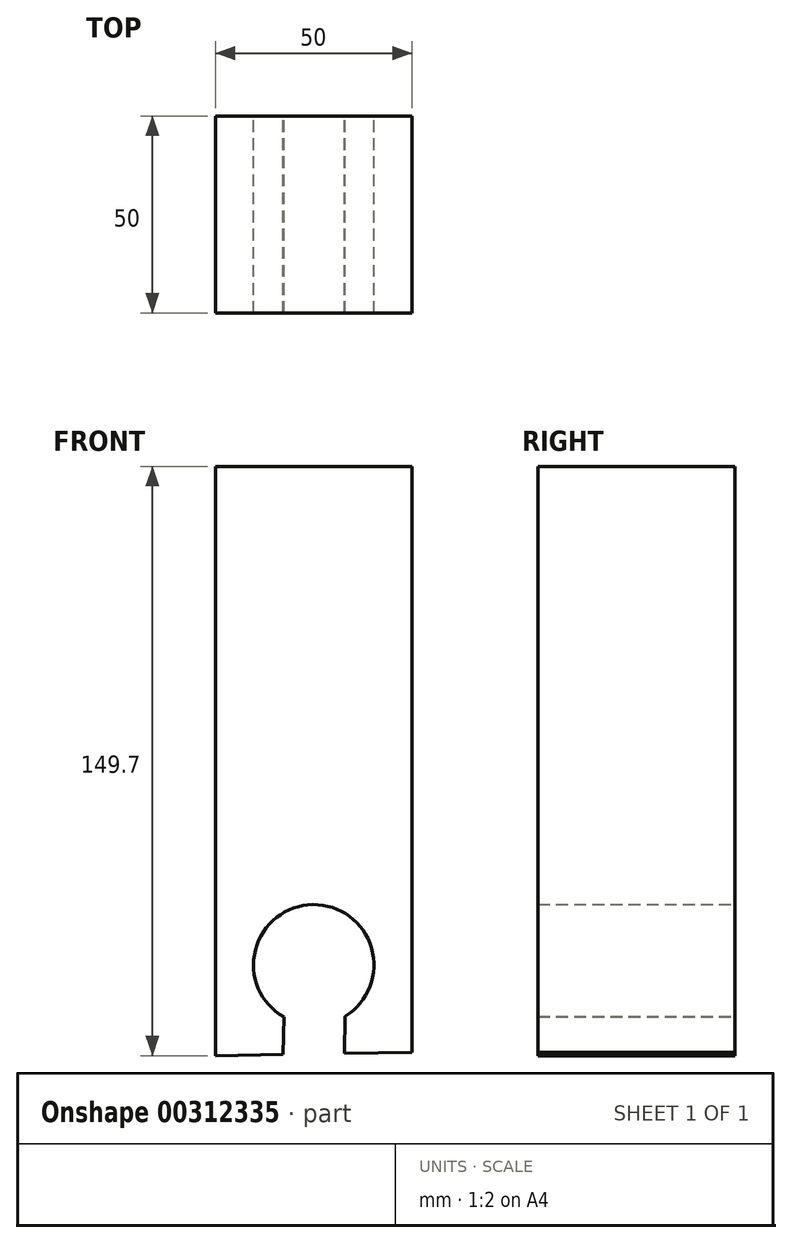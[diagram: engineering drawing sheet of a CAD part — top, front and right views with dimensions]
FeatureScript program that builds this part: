
annotation { "Feature Type Name" : "Feature", "Feature Type Description" : "" }
export const myFeature = defineFeature(function(context is Context, id is Id, definition is map)
    precondition{}
    {
        {
            var Q0;
            Q0=qCreatedBy(makeId("Front.planeOp"),FACE);
            var sketch = newSketch(context, id + "F0", { "sketchPlane" : qUnion([Q0])});
            skLineSegment(sketch, "E0.top", {"start": v(0, -120) * mm, "end": v(50, -120) * mm});
            skLineSegment(sketch, "E1", {"start": v(25, 0.4) * mm, "end": v(24.85, 10) * mm, "construction": true});
            skPoint(sketch, "E2.middle", {"position": v(25, 0.4) * mm});
            skPoint(sketch, "E3.orphan", {"position": v(32.3, -9.48) * mm});
            skPoint(sketch, "E4.orphan", {"position": v(17.29, -9.72) * mm});
            skPoint(sketch, "E5.third.point", {"position": v(24.85, 38.38) * mm});
            skLineSegment(sketch, "E6", {"start": v(0, 23.38) * mm, "end": v(50, 23.38) * mm, "construction": true});
            skLineSegment(sketch, "E7.0", {"start": v(32.81, 0.83) * mm, "end": v(50, 1.1) * mm});
            skLineSegment(sketch, "E7.1", {"start": v(0, 0.3) * mm, "end": v(17.2, 0.58) * mm});
            skLineSegment(sketch, "E7.2", {"start": v(17.4, 10.1) * mm, "end": v(17.2, 0.58) * mm});
            skArc(sketch, "E7.3", {"start": v(33, 10.35) * mm, "mid": v(24.76, 38.68) * mm, "end": v(17.4, 10.1) * mm});
            skLineSegment(sketch, "E7.4", {"start": v(33, 10.35) * mm, "end": v(32.81, 0.83) * mm});
            skLineSegment(sketch, "E8", {"start": v(0, 0) * mm, "end": v(0, 150) * mm});
            skLineSegment(sketch, "E9", {"start": v(0, 150) * mm, "end": v(50, 150) * mm});
            skLineSegment(sketch, "E10", {"start": v(50, 150) * mm, "end": v(50, 1.1) * mm});
            skSolve(sketch);
        }
        {
            var Q0;
            Q0=makeQuery(id+"F0.imprint","IMPRINT",FACE,{"disambiguationData":[TD([[makeQuery(id+"F0.imprint","IMPRINT",EDGE,{"derivedFrom":sQuery(id+"F0.wireOp",EDGE,"E7.0")}),1.0]])]});
            extrude(context, id + "F1", {"entities" : qUnion([Q0]), "depth" : 50 * mm});
        }
    });
